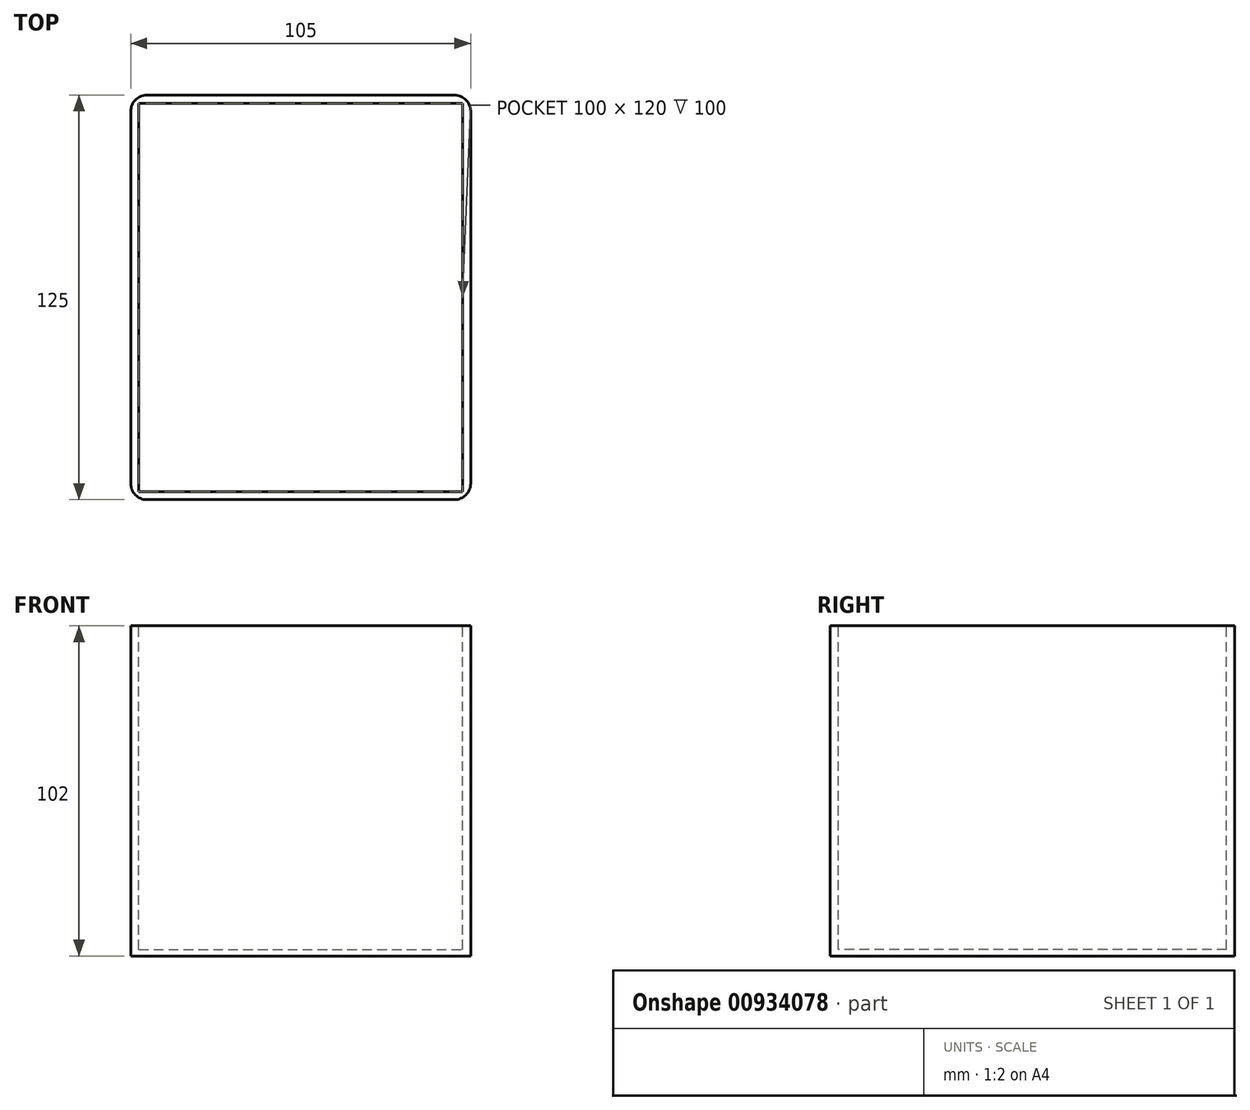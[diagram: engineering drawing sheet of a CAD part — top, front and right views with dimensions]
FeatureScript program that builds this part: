
annotation { "Feature Type Name" : "Feature", "Feature Type Description" : "" }
export const myFeature = defineFeature(function(context is Context, id is Id, definition is map)
    precondition{}
    {
        {
            var Q0;
            Q0=qCreatedBy(makeId("Top.planeOp"),FACE);
            var sketch = newSketch(context, id + "F0", { "sketchPlane" : qUnion([Q0])});
            skLineSegment(sketch, "E0.bottom", {"start": v(-52.5, 62.5) * mm, "end": v(52.5, 62.5) * mm});
            skLineSegment(sketch, "E0.top", {"start": v(-52.5, -62.5) * mm, "end": v(52.5, -62.5) * mm});
            skLineSegment(sketch, "E0.left", {"start": v(-52.5, 62.5) * mm, "end": v(-52.5, -62.5) * mm});
            skLineSegment(sketch, "E0.right", {"start": v(52.5, 62.5) * mm, "end": v(52.5, -62.5) * mm});
            skPoint(sketch, "E0.middle", {"position": v(0, 0) * mm});
            skSolve(sketch);
        }
        {
            var Q0;
            Q0 = qSketchRegion(id + "F0", true);
            extrude(context, id + "F1", {"entities" : qUnion([Q0]), "depth" : 102 * mm, "offsetDistance" : 25 * mm});
        }
        {
            var Q0;
            Q0=makeQuery(id+"F1.opExtrude","CAP_FACE",FACE,{"disambiguationData":[OSD([sQuery(id+"F0.wireOp",EDGE,"E0.bottom"),sQuery(id+"F0.wireOp",EDGE,"E0.top"),sQuery(id+"F0.wireOp",EDGE,"E0.left"),sQuery(id+"F0.wireOp",EDGE,"E0.right")])],"isStart":false});
            var sketch = newSketch(context, id + "F2", { "sketchPlane" : qUnion([Q0])});
            skLineSegment(sketch, "E1.bottom", {"start": v(-50, 60) * mm, "end": v(50, 60) * mm});
            skLineSegment(sketch, "E1.top", {"start": v(-50, -60) * mm, "end": v(50, -60) * mm});
            skLineSegment(sketch, "E1.left", {"start": v(-50, 60) * mm, "end": v(-50, -60) * mm});
            skLineSegment(sketch, "E1.right", {"start": v(50, 60) * mm, "end": v(50, -60) * mm});
            skPoint(sketch, "E1.middle", {"position": v(0, 0) * mm});
            skSolve(sketch);
        }
        {
            var Q0;
            Q0=makeQuery(id+"F2.imprint","IMPRINT",FACE,{"disambiguationData":[TD([[makeQuery(id+"F2.imprint","IMPRINT",EDGE,{"derivedFrom":sQuery(id+"F2.wireOp",EDGE,"E1.bottom")}),-1.0]])]});
            extrude(context, id + "F3", {"entities" : qUnion([Q0]), "operationType" : NewBodyOperationType.REMOVE, "oppositeDirection" : true, "depth" : 100 * mm, "offsetDistance" : 25 * mm});
        }
        {
            var Q0;
            Q0=makeQuery(id+"F1.opExtrude","SWEPT_EDGE",EDGE,{"disambiguationData":[OSD([sQuery(id+"F0.wireOp",EDGE,"E0.bottom"),sQuery(id+"F0.wireOp",EDGE,"E0.right")])]});
            var Q1;
            Q1=makeQuery(id+"F1.opExtrude","SWEPT_EDGE",EDGE,{"disambiguationData":[OSD([sQuery(id+"F0.wireOp",EDGE,"E0.top"),sQuery(id+"F0.wireOp",EDGE,"E0.right")])]});
            var Q2;
            Q2=makeQuery(id+"F1.opExtrude","SWEPT_EDGE",EDGE,{"disambiguationData":[OSD([sQuery(id+"F0.wireOp",EDGE,"E0.bottom"),sQuery(id+"F0.wireOp",EDGE,"E0.left")])]});
            var Q3;
            Q3=makeQuery(id+"F1.opExtrude","SWEPT_EDGE",EDGE,{"disambiguationData":[OSD([sQuery(id+"F0.wireOp",EDGE,"E0.top"),sQuery(id+"F0.wireOp",EDGE,"E0.left")])]});
            fillet(context, id + "F4", {"entities" : qUnion([Q0, Q1, Q2, Q3]), "radius" : 5 * mm, "tangentPropagation" : true, "allowEdgeOverflow" : false});
        }
    });
